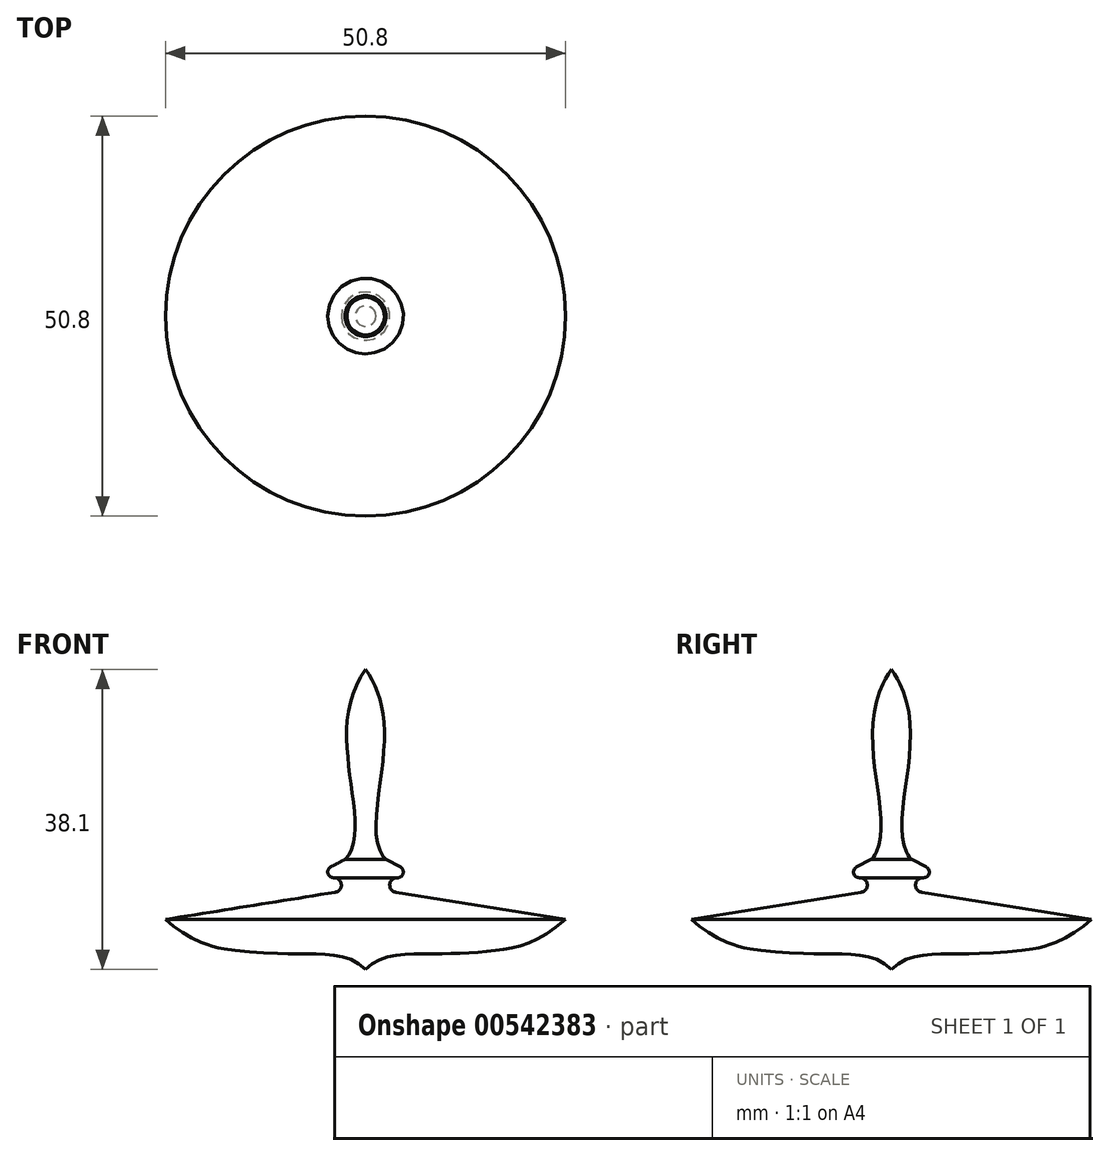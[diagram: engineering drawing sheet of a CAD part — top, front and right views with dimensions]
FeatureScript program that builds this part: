
annotation { "Feature Type Name" : "Feature", "Feature Type Description" : "" }
export const myFeature = defineFeature(function(context is Context, id is Id, definition is map)
    precondition{}
    {
        {
            var Q0;
            Q0=qCreatedBy(makeId("Front.planeOp"),FACE);
            var sketch = newSketch(context, id + "F0", { "sketchPlane" : qUnion([Q0])});
            skFitSpline(sketch, "E0", {"points": [v(0, 0) * mm, v(7.66, 1.98) * mm, v(16.35, 2.38) * mm, v(25.4, 6.35) * mm], "startDerivative": vector(18.36, 18.77) * mm, "endDerivative": vector(29.32, 25.59) * mm});
            skLineSegment(sketch, "E1", {"start": v(25.4, 6.35) * mm, "end": v(3.85, 9.8) * mm});
            skArc(sketch, "E2", {"start": v(3.85, 9.8) * mm, "mid": v(3.07, 10.82) * mm, "end": v(4.04, 11.65) * mm});
            skArc(sketch, "E3", {"start": v(4.04, 11.65) * mm, "mid": v(4.78, 12.18) * mm, "end": v(4.42, 13.01) * mm});
            skLineSegment(sketch, "E4", {"start": v(4.42, 13.01) * mm, "end": v(2.6, 13.98) * mm});
            skFitSpline(sketch, "E5", {"points": [v(2.6, 13.98) * mm, v(1.4, 16.78) * mm, v(1.95, 24.28) * mm, v(2.34, 31.52) * mm, v(1.4, 35.47) * mm, v(0, 38.1) * mm], "startDerivative": vector(-9.6, 4.61) * mm, "endDerivative": vector(-9.55, 13.04) * mm});
            skLineSegment(sketch, "E6", {"start": v(0, 38.1) * mm, "end": v(0, 0) * mm});
            skLineSegment(sketch, "E7", {"start": v(0, -11.77) * mm, "end": v(0, 42.26) * mm});
            skSolve(sketch);
        }
        {
            var Q0;
            {var subQ0=sQuery(id+"F0.wireOp",EDGE,"E0");Q0=makeQuery(id+"F0.imprint","IMPRINT",FACE,{"disambiguationData":[TD([[makeQuery(id+"F0.imprint","IMPRINT",EDGE,{"derivedFrom":subQ0}),1.0]])]});}
            var Q1;
            Q1=sQuery(id+"F0.wireOp",EDGE,"E7");
            revolve(context, id + "F1", {"entities" : qUnion([Q0]), "axis" : qUnion([Q1]), "revolveType" : RevolveType.FULL});
        }
    });
